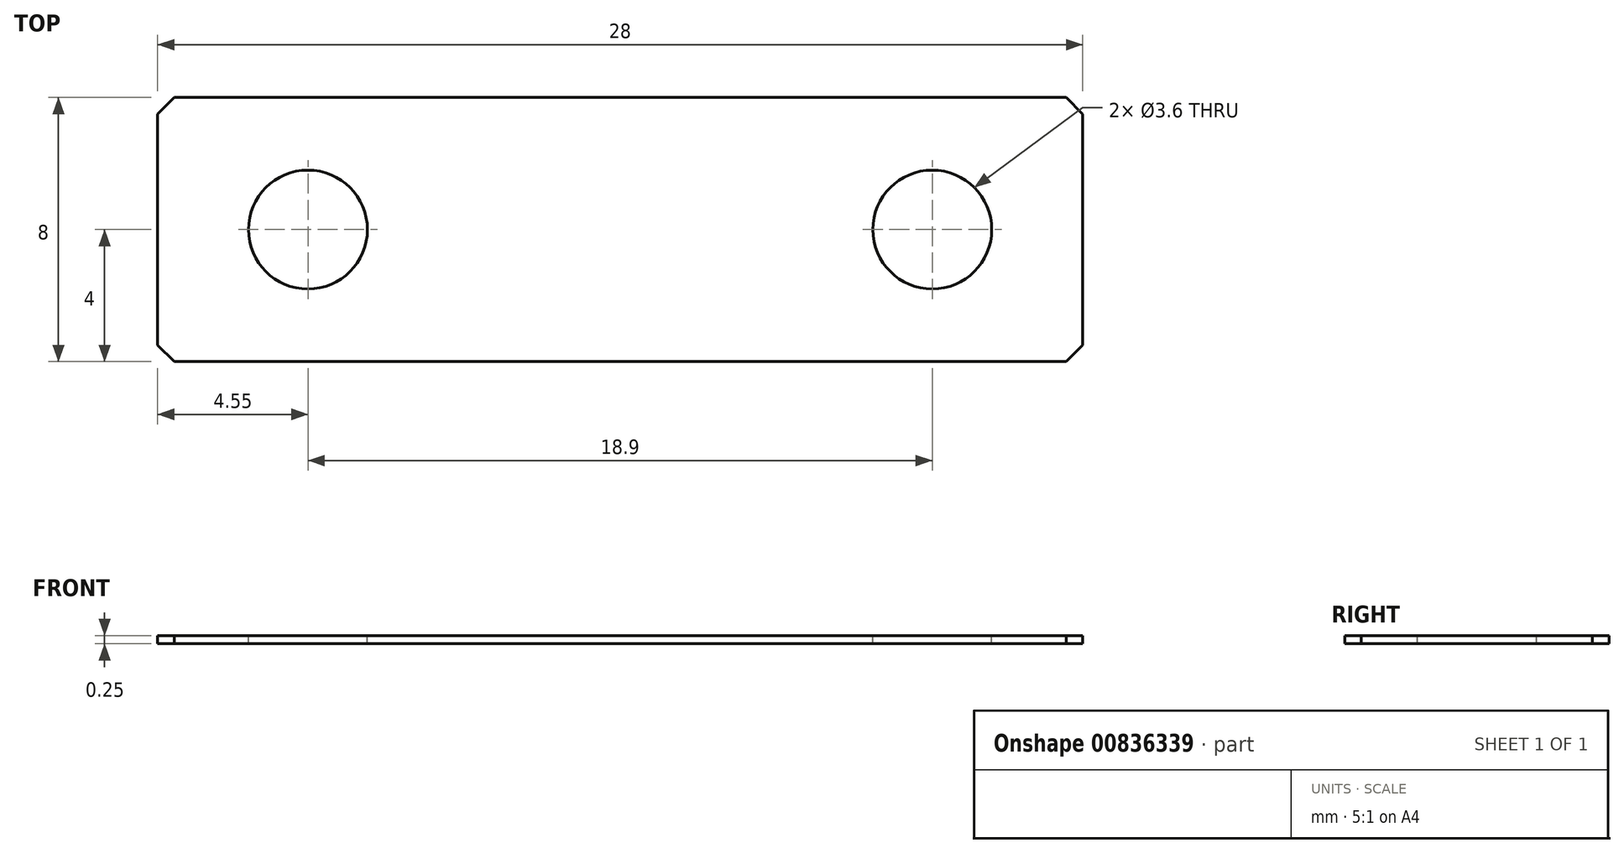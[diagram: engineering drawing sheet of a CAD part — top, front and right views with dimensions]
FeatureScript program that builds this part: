
annotation { "Feature Type Name" : "Feature", "Feature Type Description" : "" }
export const myFeature = defineFeature(function(context is Context, id is Id, definition is map)
    precondition{}
    {
        {
            var Q0;
            Q0=qCreatedBy(makeId("Top.planeOp"),FACE);
            var sketch = newSketch(context, id + "F0", { "sketchPlane" : qUnion([Q0])});
            skLineSegment(sketch, "E0.bottom", {"start": v(14, -4) * mm, "end": v(-14, -4) * mm});
            skLineSegment(sketch, "E0.top", {"start": v(14, 4) * mm, "end": v(-14, 4) * mm});
            skLineSegment(sketch, "E0.left", {"start": v(14, -4) * mm, "end": v(14, 4) * mm});
            skLineSegment(sketch, "E0.right", {"start": v(-14, -4) * mm, "end": v(-14, 4) * mm});
            skPoint(sketch, "E0.middle", {"position": v(0, 0) * mm});
            skSolve(sketch);
        }
        {
            var Q0;
            Q0=makeQuery(id+"F0.imprint","IMPRINT",FACE,{"disambiguationData":[TD([[makeQuery(id+"F0.imprint","IMPRINT",EDGE,{"derivedFrom":sQuery(id+"F0.wireOp",EDGE,"E0.bottom")}),-1.0]])]});
            extrude(context, id + "F1", {"entities" : qUnion([Q0]), "depth" : .25 * mm, "offsetDistance" : 25 * mm});
        }
        {
            var Q0;
            Q0=makeQuery(id+"F1.opExtrude","SWEPT_EDGE",EDGE,{"disambiguationData":[OSD([sQuery(id+"F0.wireOp",EDGE,"E0.bottom"),sQuery(id+"F0.wireOp",EDGE,"E0.right")])]});
            var Q1;
            Q1=makeQuery(id+"F1.opExtrude","SWEPT_EDGE",EDGE,{"disambiguationData":[OSD([sQuery(id+"F0.wireOp",EDGE,"E0.top"),sQuery(id+"F0.wireOp",EDGE,"E0.right")])]});
            var Q2;
            Q2=makeQuery(id+"F1.opExtrude","SWEPT_EDGE",EDGE,{"disambiguationData":[OSD([sQuery(id+"F0.wireOp",EDGE,"E0.bottom"),sQuery(id+"F0.wireOp",EDGE,"E0.left")])]});
            var Q3;
            Q3=makeQuery(id+"F1.opExtrude","SWEPT_EDGE",EDGE,{"disambiguationData":[OSD([sQuery(id+"F0.wireOp",EDGE,"E0.top"),sQuery(id+"F0.wireOp",EDGE,"E0.left")])]});
            chamfer(context, id + "F2", {"entities" : qUnion([Q0, Q1, Q2, Q3]), "width" : 0.5 * mm, "tangentPropagation" : true});
        }
        {
            var Q0;
            Q0=makeQuery(id+"F1.opExtrude","CAP_FACE",FACE,{"disambiguationData":[OSD([sQuery(id+"F0.wireOp",EDGE,"E0.bottom"),sQuery(id+"F0.wireOp",EDGE,"E0.top"),sQuery(id+"F0.wireOp",EDGE,"E0.left"),sQuery(id+"F0.wireOp",EDGE,"E0.right")])],"isStart":false});
            var sketch = newSketch(context, id + "F3", { "sketchPlane" : qUnion([Q0])});
            skLineSegment(sketch, "E1", {"start": v(0, 0) * mm, "end": v(0, 6.66) * mm, "construction": true});
            skPoint(sketch, "E1.endSnap0", {"position": v(0, 4) * mm});
            skCircle(sketch, "E2", {"center": v(-9.45, 0) * mm, "radius": 1.8 * mm});
            skCircle(sketch, "E3", {"center": v(9.45, 0) * mm, "radius": 1.8 * mm});
            skLineSegment(sketch, "E4", {"start": v(-14, 0) * mm, "end": v(14, 0) * mm, "construction": true});
            skSolve(sketch);
        }
        {
            var Q0;
            Q0=makeQuery(id+"F3.imprint","IMPRINT",FACE,{"disambiguationData":[TD([[makeQuery(id+"F3.imprint","IMPRINT",EDGE,{"derivedFrom":sQuery(id+"F3.wireOp",EDGE,"E2")}),1.0]])]});
            var Q1;
            Q1=makeQuery(id+"F3.imprint","IMPRINT",FACE,{"disambiguationData":[TD([[makeQuery(id+"F3.imprint","IMPRINT",EDGE,{"derivedFrom":sQuery(id+"F3.wireOp",EDGE,"E3")}),1.0]])]});
            extrude(context, id + "F4", {"entities" : qUnion([Q0, Q1]), "operationType" : NewBodyOperationType.REMOVE, "endBound" : BoundingType.THROUGH_ALL, "oppositeDirection" : true, "depth" : 25 * mm, "offsetDistance" : 25 * mm});
        }
    });
